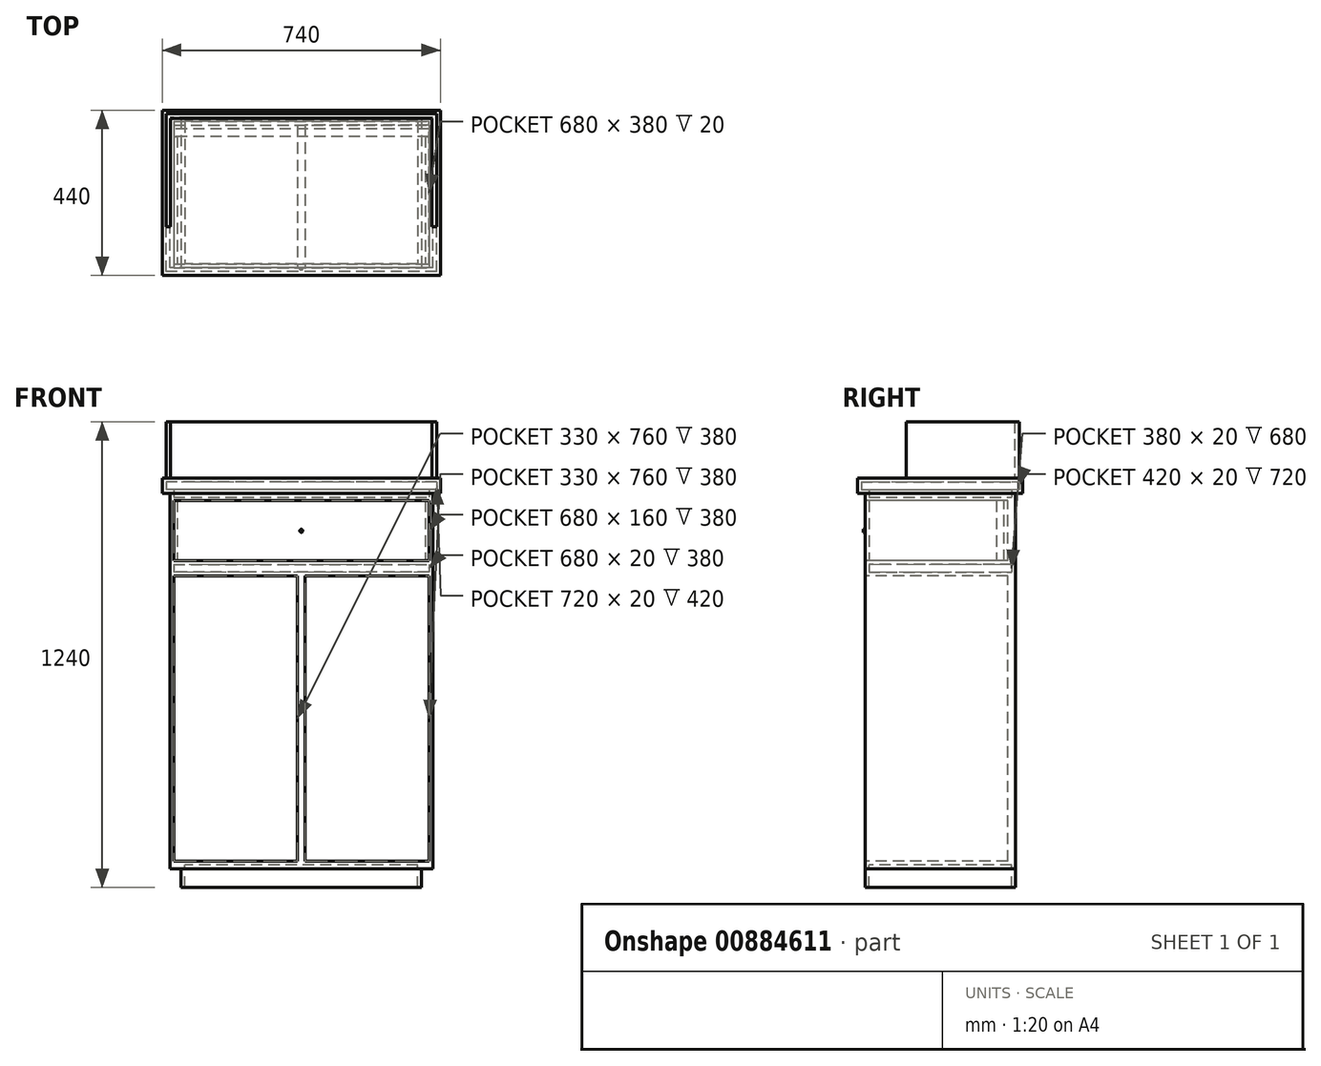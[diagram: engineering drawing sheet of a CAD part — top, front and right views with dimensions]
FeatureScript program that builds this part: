
annotation { "Feature Type Name" : "Feature", "Feature Type Description" : "" }
export const myFeature = defineFeature(function(context is Context, id is Id, definition is map)
    precondition{}
    {
        {
            var Q0;
            Q0=qCreatedBy(makeId("Top.planeOp"),FACE);
            var sketch = newSketch(context, id + "F0", { "sketchPlane" : qUnion([Q0])});
            skLineSegment(sketch, "E0.bottom", {"start": v(350, -200) * mm, "end": v(-350, -200) * mm});
            skLineSegment(sketch, "E0.top", {"start": v(350, 200) * mm, "end": v(-350, 200) * mm});
            skLineSegment(sketch, "E0.left", {"start": v(350, -200) * mm, "end": v(350, 200) * mm});
            skLineSegment(sketch, "E0.right", {"start": v(-350, -200) * mm, "end": v(-350, 200) * mm});
            skPoint(sketch, "E0.middle", {"position": v(0, 0) * mm});
            skSolve(sketch);
        }
        {
            var Q0;
            Q0 = qSketchRegion(id + "F0", true);
            extrude(context, id + "F1", {"entities" : qUnion([Q0]), "depth" : 1000 * mm, "offsetDistance" : 25 * mm});
        }
        {
            var Q0;
            Q0=makeQuery(id+"F1.opExtrude","SWEPT_FACE",FACE,{"disambiguationData":[OSD([sQuery(id+"F0.wireOp",EDGE,"E0.bottom")])]});
            var sketch = newSketch(context, id + "F2", { "sketchPlane" : qUnion([Q0])});
            skLineSegment(sketch, "E1", {"start": v(0, 1000) * mm, "end": v(0, 0) * mm, "construction": true});
            skLineSegment(sketch, "E2.bottom", {"start": v(-340, 20) * mm, "end": v(-10, 20) * mm});
            skLineSegment(sketch, "E2.top", {"start": v(-340, 780) * mm, "end": v(-10, 780) * mm});
            skLineSegment(sketch, "E2.left", {"start": v(-340, 20) * mm, "end": v(-340, 780) * mm});
            skLineSegment(sketch, "E2.right", {"start": v(-10, 20) * mm, "end": v(-10, 780) * mm});
            skLineSegment(sketch, "E3.MirrorCS", {"start": v(340, 780) * mm, "end": v(10, 780) * mm});
            skLineSegment(sketch, "E4.MirrorCS", {"start": v(10, 20) * mm, "end": v(10, 780) * mm});
            skLineSegment(sketch, "E5.MirrorCS", {"start": v(340, 20) * mm, "end": v(10, 20) * mm});
            skLineSegment(sketch, "E6.MirrorCS", {"start": v(340, 20) * mm, "end": v(340, 780) * mm});
            skLineSegment(sketch, "E7.bottom", {"start": v(-340, 820) * mm, "end": v(340, 820) * mm});
            skLineSegment(sketch, "E7.top", {"start": v(-340, 980) * mm, "end": v(340, 980) * mm});
            skLineSegment(sketch, "E7.left", {"start": v(-340, 820) * mm, "end": v(-340, 980) * mm});
            skLineSegment(sketch, "E7.right", {"start": v(340, 820) * mm, "end": v(340, 980) * mm});
            skSolve(sketch);
        }
        {
            var Q0;
            Q0 = qSketchRegion(id + "F2", true);
            extrude(context, id + "F3", {"entities" : qUnion([Q0]), "operationType" : NewBodyOperationType.REMOVE, "oppositeDirection" : true, "depth" : 380 * mm, "offsetDistance" : 25 * mm});
        }
        {
            var Q0;
            Q0=makeQuery(id+"F1.opExtrude","SWEPT_FACE",FACE,{"disambiguationData":[OSD([sQuery(id+"F0.wireOp",EDGE,"E0.bottom")])]});
            var sketch = newSketch(context, id + "F4", { "sketchPlane" : qUnion([Q0])});
            skLineSegment(sketch, "E8.bottom", {"start": v(-340, 980) * mm, "end": v(340, 980) * mm});
            skLineSegment(sketch, "E8.top", {"start": v(-340, 820) * mm, "end": v(340, 820) * mm});
            skLineSegment(sketch, "E8.left", {"start": v(-340, 980) * mm, "end": v(-340, 820) * mm});
            skLineSegment(sketch, "E8.right", {"start": v(340, 980) * mm, "end": v(340, 820) * mm});
            skSolve(sketch);
        }
        {
            var Q0;
            Q0 = qSketchRegion(id + "F4", true);
            extrude(context, id + "F5", {"entities" : qUnion([Q0]), "oppositeDirection" : true, "depth" : 10 * mm, "offsetDistance" : 25 * mm});
        }
        {
            var Q0;
            Q0=makeQuery(id+"F5.opExtrude","CAP_FACE",FACE,{"disambiguationData":[OSD([sQuery(id+"F4.wireOp",EDGE,"E8.bottom"),sQuery(id+"F4.wireOp",EDGE,"E8.top"),sQuery(id+"F4.wireOp",EDGE,"E8.left"),sQuery(id+"F4.wireOp",EDGE,"E8.right")])],"isStart":false});
            var sketch = newSketch(context, id + "F6", { "sketchPlane" : qUnion([Q0])});
            skLineSegment(sketch, "E9.bottom", {"start": v(-340, 980) * mm, "end": v(-330, 980) * mm});
            skLineSegment(sketch, "E9.top", {"start": v(-340, 820) * mm, "end": v(-330, 820) * mm});
            skLineSegment(sketch, "E9.left", {"start": v(-340, 980) * mm, "end": v(-340, 820) * mm});
            skLineSegment(sketch, "E9.right", {"start": v(-330, 980) * mm, "end": v(-330, 820) * mm});
            skLineSegment(sketch, "E10", {"start": v(0, 980) * mm, "end": v(0, 820) * mm, "construction": true});
            skLineSegment(sketch, "E11.MirrorCS", {"start": v(340, 980) * mm, "end": v(330, 980) * mm});
            skLineSegment(sketch, "E12.MirrorCS", {"start": v(330, 980) * mm, "end": v(330, 820) * mm});
            skLineSegment(sketch, "E13.MirrorCS", {"start": v(340, 980) * mm, "end": v(340, 820) * mm});
            skLineSegment(sketch, "E14.MirrorCS", {"start": v(340, 820) * mm, "end": v(330, 820) * mm});
            skSolve(sketch);
        }
        {
            var Q0;
            Q0 = qSketchRegion(id + "F6", true);
            extrude(context, id + "F7", {"entities" : qUnion([Q0]), "depth" : 340 * mm, "offsetDistance" : 25 * mm});
        }
        {
            var Q0;
            Q0=makeQuery(id+"F7.opExtrude","CAP_FACE",FACE,{"disambiguationData":[OSD([sQuery(id+"F6.wireOp",EDGE,"E9.bottom"),sQuery(id+"F6.wireOp",EDGE,"E9.top"),sQuery(id+"F6.wireOp",EDGE,"E9.left"),sQuery(id+"F6.wireOp",EDGE,"E9.right")])],"isStart":false});
            var sketch = newSketch(context, id + "F8", { "sketchPlane" : qUnion([Q0])});
            skLineSegment(sketch, "E15.bottom", {"start": v(-340, 980) * mm, "end": v(340, 980) * mm});
            skLineSegment(sketch, "E15.top", {"start": v(-340, 820) * mm, "end": v(340, 820) * mm});
            skLineSegment(sketch, "E15.left", {"start": v(-340, 980) * mm, "end": v(-340, 820) * mm});
            skLineSegment(sketch, "E15.right", {"start": v(340, 980) * mm, "end": v(340, 820) * mm});
            skSolve(sketch);
        }
        {
            var Q0;
            Q0 = qSketchRegion(id + "F8", true);
            extrude(context, id + "F9", {"entities" : qUnion([Q0]), "depth" : 20 * mm, "offsetDistance" : 25 * mm});
        }
        {
            var Q0;
            Q0=makeQuery(id+"F5.opExtrude","CAP_FACE",FACE,{"disambiguationData":[OSD([sQuery(id+"F4.wireOp",EDGE,"E8.bottom"),sQuery(id+"F4.wireOp",EDGE,"E8.top"),sQuery(id+"F4.wireOp",EDGE,"E8.left"),sQuery(id+"F4.wireOp",EDGE,"E8.right")])],"isStart":true});
            var sketch = newSketch(context, id + "F10", { "sketchPlane" : qUnion([Q0])});
            skLineSegment(sketch, "E16", {"start": v(-340, 900) * mm, "end": v(340, 900) * mm, "construction": true});
            skLineSegment(sketch, "E17", {"start": v(0, 980) * mm, "end": v(0, 820) * mm, "construction": true});
            skCircle(sketch, "E18", {"center": v(0, 900) * mm, "radius": 4 * mm});
            skSolve(sketch);
        }
        {
            var Q0;
            Q0 = qSketchRegion(id + "F10", true);
            extrude(context, id + "F11", {"entities" : qUnion([Q0]), "depth" : 5 * mm, "offsetDistance" : 25 * mm});
        }
        {
            var Q0;
            Q0 = qSketchRegion(id + "F10", true);
            extrude(context, id + "F12", {"entities" : qUnion([Q0]), "depth" : 5 * mm, "offsetDistance" : 25 * mm});
        }
        {
            var Q0;
            Q0=makeQuery(id+"F1.opExtrude","CAP_FACE",FACE,{"disambiguationData":[OSD([sQuery(id+"F0.wireOp",EDGE,"E0.bottom"),sQuery(id+"F0.wireOp",EDGE,"E0.top"),sQuery(id+"F0.wireOp",EDGE,"E0.left"),sQuery(id+"F0.wireOp",EDGE,"E0.right")])],"isStart":false});
            var sketch = newSketch(context, id + "F13", { "sketchPlane" : qUnion([Q0])});
            skLineSegment(sketch, "E19.bottom", {"start": v(370, -220) * mm, "end": v(-370, -220) * mm});
            skLineSegment(sketch, "E19.top", {"start": v(370, 220) * mm, "end": v(-370, 220) * mm});
            skLineSegment(sketch, "E19.left", {"start": v(370, -220) * mm, "end": v(370, 220) * mm});
            skLineSegment(sketch, "E19.right", {"start": v(-370, -220) * mm, "end": v(-370, 220) * mm});
            skPoint(sketch, "E19.middle", {"position": v(0, 0) * mm});
            skSolve(sketch);
        }
        {
            var Q0;
            Q0 = qSketchRegion(id + "F13", true);
            extrude(context, id + "F14", {"entities" : qUnion([Q0]), "operationType" : NewBodyOperationType.ADD, "depth" : 40 * mm, "offsetDistance" : 25 * mm});
        }
        {
            var Q0;
            Q0=makeQuery(id+"F1.opExtrude","CAP_FACE",FACE,{"disambiguationData":[OSD([sQuery(id+"F0.wireOp",EDGE,"E0.bottom"),sQuery(id+"F0.wireOp",EDGE,"E0.top"),sQuery(id+"F0.wireOp",EDGE,"E0.left"),sQuery(id+"F0.wireOp",EDGE,"E0.right")])],"isStart":true});
            var sketch = newSketch(context, id + "F15", { "sketchPlane" : qUnion([Q0])});
            skLineSegment(sketch, "E20.bottom", {"start": v(320, -199.88) * mm, "end": v(-320, -199.88) * mm});
            skLineSegment(sketch, "E20.top", {"start": v(320, 199.88) * mm, "end": v(-320, 199.88) * mm});
            skLineSegment(sketch, "E20.left", {"start": v(320, -199.88) * mm, "end": v(320, 199.88) * mm});
            skLineSegment(sketch, "E20.right", {"start": v(-320, -199.88) * mm, "end": v(-320, 199.88) * mm});
            skPoint(sketch, "E20.middle", {"position": v(0, 0) * mm});
            skSolve(sketch);
        }
        {
            var Q0;
            Q0 = qSketchRegion(id + "F15", true);
            extrude(context, id + "F16", {"entities" : qUnion([Q0]), "operationType" : NewBodyOperationType.ADD, "depth" : 50 * mm, "offsetDistance" : 25 * mm});
        }
        {
            var Q0;
            Q0=makeQuery(id+"F16.opExtrude","CAP_FACE",FACE,{"disambiguationData":[OSD([sQuery(id+"F15.wireOp",EDGE,"E20.bottom"),sQuery(id+"F15.wireOp",EDGE,"E20.top"),sQuery(id+"F15.wireOp",EDGE,"E20.left"),sQuery(id+"F15.wireOp",EDGE,"E20.right")])],"isStart":false});
            shell(context, id + "F17", {"entities" : qUnion([Q0]), "thickness" : 10 * mm});
        }
        {
            var Q0;
            Q0=makeQuery(id+"F14.opExtrude","CAP_FACE",FACE,{"disambiguationData":[OSD([sQuery(id+"F13.wireOp",EDGE,"E19.bottom"),sQuery(id+"F13.wireOp",EDGE,"E19.top"),sQuery(id+"F13.wireOp",EDGE,"E19.left"),sQuery(id+"F13.wireOp",EDGE,"E19.right")])],"isStart":false});
            var sketch = newSketch(context, id + "F18", { "sketchPlane" : qUnion([Q0])});
            skLineSegment(sketch, "E21.bottom", {"start": v(348, 198) * mm, "end": v(-348, 198) * mm});
            skLineSegment(sketch, "E21.top", {"start": v(360, 210) * mm, "end": v(-360, 210) * mm});
            skLineSegment(sketch, "E21.left", {"start": v(360, 198) * mm, "end": v(360, 210) * mm});
            skLineSegment(sketch, "E21.right", {"start": v(-360, 198) * mm, "end": v(-360, 210) * mm});
            skPoint(sketch, "E21.middle", {"position": v(0, 204) * mm});
            skLineSegment(sketch, "E22.bottom", {"start": v(-360, 210) * mm, "end": v(-348, 210) * mm});
            skLineSegment(sketch, "E22.top", {"start": v(-360, -90) * mm, "end": v(-348, -90) * mm});
            skLineSegment(sketch, "E22.left", {"start": v(-360, 210) * mm, "end": v(-360, -90) * mm});
            skLineSegment(sketch, "E22.right", {"start": v(-348, 198) * mm, "end": v(-348, -90) * mm});
            skLineSegment(sketch, "E23", {"start": v(0, 0) * mm, "end": v(0, 262.5) * mm, "construction": true});
            skLineSegment(sketch, "E24.MirrorCS", {"start": v(360, 210) * mm, "end": v(360, -90) * mm});
            skLineSegment(sketch, "E25.MirrorCS", {"start": v(348, 198) * mm, "end": v(348, -90) * mm});
            skLineSegment(sketch, "E26.MirrorCS", {"start": v(360, 210) * mm, "end": v(348, 210) * mm});
            skLineSegment(sketch, "E27.MirrorCS", {"start": v(360, -90) * mm, "end": v(348, -90) * mm});
            skPoint(sketch, "E28.orphan", {"position": v(348, 210) * mm});
            skSolve(sketch);
        }
        {
            var Q0;
            Q0 = qSketchRegion(id + "F18", true);
            extrude(context, id + "F19", {"entities" : qUnion([Q0]), "operationType" : NewBodyOperationType.ADD, "depth" : 150 * mm, "offsetDistance" : 25 * mm});
        }
    });
